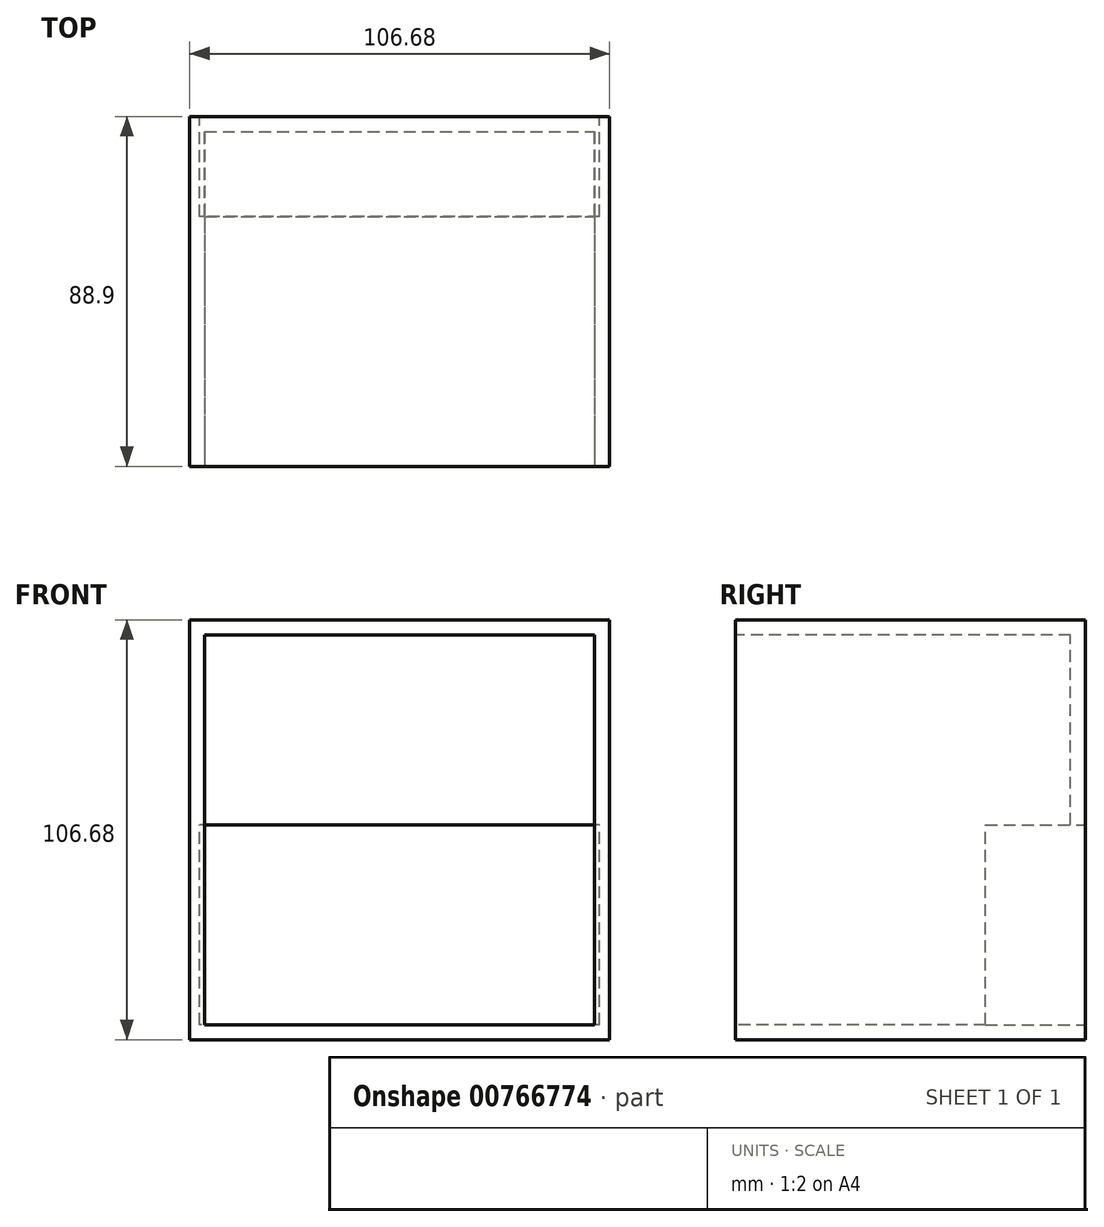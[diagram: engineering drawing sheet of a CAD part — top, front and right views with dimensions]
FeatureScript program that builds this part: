
annotation { "Feature Type Name" : "Feature", "Feature Type Description" : "" }
export const myFeature = defineFeature(function(context is Context, id is Id, definition is map)
    precondition{}
    {
        {
            var Q0;
            Q0=qCreatedBy(makeId("Front.planeOp"),FACE);
            var sketch = newSketch(context, id + "F0", { "sketchPlane" : qUnion([Q0])});
            skLineSegment(sketch, "E0.bottom", {"start": v(0, 0) * mm, "end": v(106.68, 0) * mm});
            skLineSegment(sketch, "E0.top", {"start": v(0, 106.68) * mm, "end": v(106.68, 106.68) * mm});
            skLineSegment(sketch, "E0.left", {"start": v(0, 0) * mm, "end": v(0, 106.68) * mm});
            skLineSegment(sketch, "E0.right", {"start": v(106.68, 0) * mm, "end": v(106.68, 106.68) * mm});
            skSolve(sketch);
        }
        {
            var Q0;
            Q0=makeQuery(id+"F0.imprint","IMPRINT",FACE,{"disambiguationData":[TD([[makeQuery(id+"F0.imprint","IMPRINT",EDGE,{"derivedFrom":sQuery(id+"F0.wireOp",EDGE,"E0.bottom")}),1.0]])]});
            extrude(context, id + "F1", {"entities" : qUnion([Q0]), "oppositeDirection" : true, "depth" : 88.9 * mm, "offsetDistance" : 25.4 * mm});
        }
        {
            var Q0;
            Q0=makeQuery(id+"F1.opExtrude","CAP_FACE",FACE,{"disambiguationData":[OSD([sQuery(id+"F0.wireOp",EDGE,"E0.bottom"),sQuery(id+"F0.wireOp",EDGE,"E0.top"),sQuery(id+"F0.wireOp",EDGE,"E0.left"),sQuery(id+"F0.wireOp",EDGE,"E0.right")])],"isStart":true});
            shell(context, id + "F2", {"entities" : qUnion([Q0]), "thickness" : 3.8 * mm});
        }
        {
            var Q0;
            Q0=makeQuery(id+"F1.opExtrude","CAP_FACE",FACE,{"disambiguationData":[OSD([sQuery(id+"F0.wireOp",EDGE,"E0.bottom"),sQuery(id+"F0.wireOp",EDGE,"E0.top"),sQuery(id+"F0.wireOp",EDGE,"E0.left"),sQuery(id+"F0.wireOp",EDGE,"E0.right")])],"isStart":false});
            var sketch = newSketch(context, id + "F3", { "sketchPlane" : qUnion([Q0])});
            skLineSegment(sketch, "E1.bottom", {"start": v(-104.14, 3.78) * mm, "end": v(-2.54, 3.78) * mm});
            skLineSegment(sketch, "E1.top", {"start": v(-104.14, 54.58) * mm, "end": v(-2.54, 54.58) * mm});
            skLineSegment(sketch, "E1.left", {"start": v(-104.14, 3.78) * mm, "end": v(-104.14, 54.58) * mm});
            skLineSegment(sketch, "E1.right", {"start": v(-2.54, 3.78) * mm, "end": v(-2.54, 54.58) * mm});
            skSolve(sketch);
        }
        {
            var Q0;
            Q0=makeQuery(id+"F3.imprint","IMPRINT",FACE,{"disambiguationData":[TD([[makeQuery(id+"F3.imprint","IMPRINT",EDGE,{"derivedFrom":sQuery(id+"F3.wireOp",EDGE,"E1.bottom")}),1.0]])]});
            extrude(context, id + "F4", {"entities" : qUnion([Q0]), "operationType" : NewBodyOperationType.REMOVE, "oppositeDirection" : true, "depth" : 25.4 * mm, "offsetDistance" : 25.4 * mm});
        }
    });
